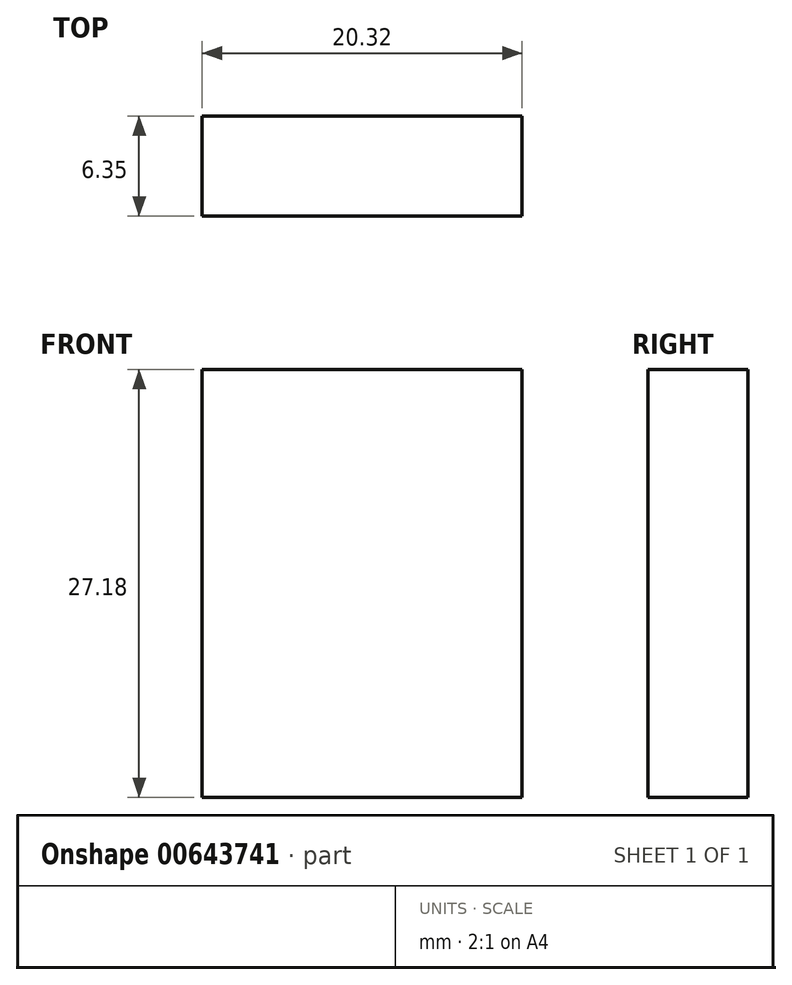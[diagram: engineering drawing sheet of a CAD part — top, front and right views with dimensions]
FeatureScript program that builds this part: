
annotation { "Feature Type Name" : "Feature", "Feature Type Description" : "" }
export const myFeature = defineFeature(function(context is Context, id is Id, definition is map)
    precondition{}
    {
        {
            var Q0;
            Q0=qCreatedBy(makeId("Front.planeOp"),FACE);
            var sketch = newSketch(context, id + "F0", { "sketchPlane" : qUnion([Q0])});
            skLineSegment(sketch, "E0.bottom", {"start": v(10.16, 13.59) * mm, "end": v(-10.16, 13.59) * mm});
            skLineSegment(sketch, "E0.top", {"start": v(10.16, -13.59) * mm, "end": v(-10.16, -13.59) * mm});
            skLineSegment(sketch, "E0.left", {"start": v(10.16, 13.59) * mm, "end": v(10.16, -13.59) * mm});
            skLineSegment(sketch, "E0.right", {"start": v(-10.16, 13.59) * mm, "end": v(-10.16, -13.59) * mm});
            skPoint(sketch, "E0.middle", {"position": v(0, 0) * mm});
            skSolve(sketch);
        }
        {
            var Q0;
            Q0 = qSketchRegion(id + "F0", true);
            extrude(context, id + "F1", {"entities" : qUnion([Q0]), "depth" : 6.35 * mm, "offsetDistance" : 25.4 * mm});
        }
    });
